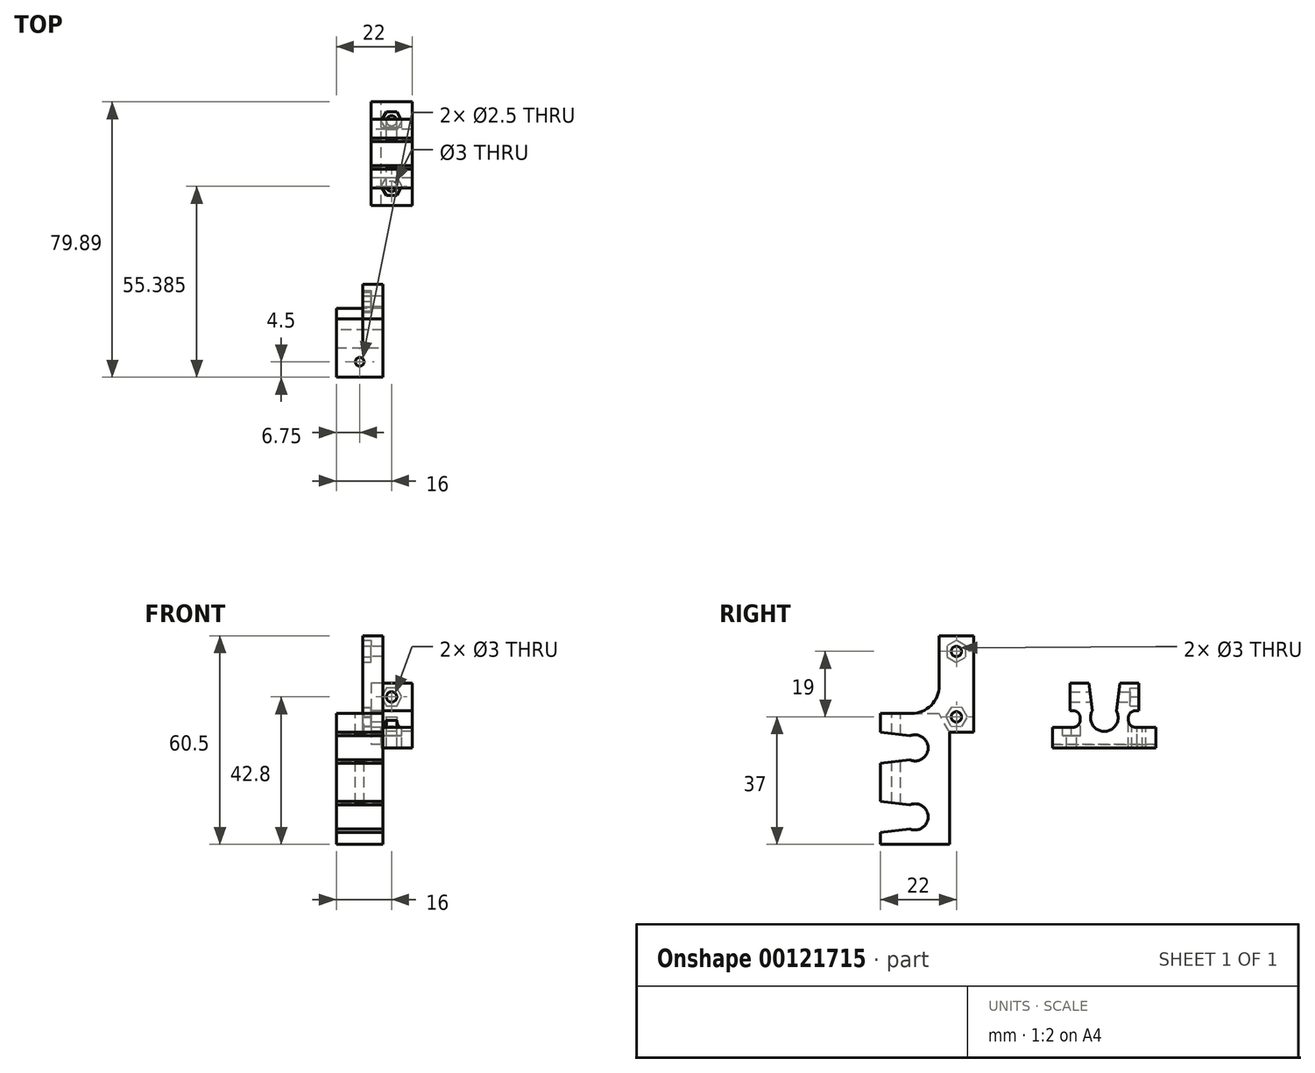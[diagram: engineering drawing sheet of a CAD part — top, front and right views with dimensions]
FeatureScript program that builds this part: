
annotation { "Feature Type Name" : "Feature", "Feature Type Description" : "" }
export const myFeature = defineFeature(function(context is Context, id is Id, definition is map)
    precondition{}
    {
        {
            var Q0;
            Q0=qCreatedBy(makeId("Right.planeOp"),FACE);
            var sketch = newSketch(context, id + "F0", { "sketchPlane" : qUnion([Q0])});
            skCircle(sketch, "E0", {"center": v(0, 0) * mm, "radius": 3.8 * mm});
            skCircle(sketch, "E1", {"center": v(0, -20) * mm, "radius": 3.8 * mm});
            skCircle(sketch, "E2", {"center": v(12, 9) * mm, "radius": 1.5 * mm});
            skCircle(sketch, "E3", {"center": v(12, 28) * mm, "radius": 1.5 * mm});
            skLineSegment(sketch, "E4", {"start": v(12, 28) * mm, "end": v(12, 9) * mm, "construction": true});
            skLineSegment(sketch, "E5.bottom", {"start": v(7, 32.5) * mm, "end": v(17, 32.5) * mm});
            skLineSegment(sketch, "E5.top", {"start": v(10, 4.5) * mm, "end": v(17, 4.5) * mm});
            skLineSegment(sketch, "E5.left", {"start": v(7, 32.5) * mm, "end": v(7, 18) * mm});
            skLineSegment(sketch, "E5.right", {"start": v(17, 32.5) * mm, "end": v(17, 4.5) * mm});
            skLineSegment(sketch, "E6.bottom", {"start": v(-10, 10) * mm, "end": v(-1, 10) * mm});
            skLineSegment(sketch, "E6.top", {"start": v(-10, -28) * mm, "end": v(10, -28) * mm});
            skLineSegment(sketch, "E6.left", {"start": v(-10, 10) * mm, "end": v(-10, -28) * mm});
            skLineSegment(sketch, "E6.right", {"start": v(10, 4.5) * mm, "end": v(10, -28) * mm});
            skPoint(sketch, "E7.visualSharp", {"position": v(7, 10) * mm});
            skArc(sketch, "E7.filletArc", {"start": v(-1, 10) * mm, "mid": v(4.66, 12.34) * mm, "end": v(7, 18) * mm});
            skLineSegment(sketch, "E8", {"start": v(0, 0) * mm, "end": v(0, -20) * mm, "construction": true});
            skSolve(sketch);
        }
        {
            var Q0;
            Q0 = qSketchRegion(id + "F0", true);
            extrude(context, id + "F1", {"entities" : qUnion([Q0]), "depth" : 3.5 * mm});
        }
        {
            var Q0;
            Q0=makeQuery(id+"F1.opExtrude","CAP_FACE",FACE,{"disambiguationData":[OSD([sQuery(id+"F0.wireOp",EDGE,"E0"),sQuery(id+"F0.wireOp",EDGE,"E1"),sQuery(id+"F0.wireOp",EDGE,"E2"),sQuery(id+"F0.wireOp",EDGE,"E3"),sQuery(id+"F0.wireOp",EDGE,"E5.bottom"),sQuery(id+"F0.wireOp",EDGE,"E5.top"),sQuery(id+"F0.wireOp",EDGE,"E5.left"),sQuery(id+"F0.wireOp",EDGE,"E5.right"),sQuery(id+"F0.wireOp",EDGE,"E6.bottom"),sQuery(id+"F0.wireOp",EDGE,"E6.top"),sQuery(id+"F0.wireOp",EDGE,"E6.left"),sQuery(id+"F0.wireOp",EDGE,"E6.right"),sQuery(id+"F0.wireOp",EDGE,"E7.filletArc")])],"isStart":true});
            var sketch = newSketch(context, id + "F2", { "sketchPlane" : qUnion([Q0])});
            skLineSegment(sketch, "E9.0", {"start": v(-10, 4.5) * mm, "end": v(-10, -28) * mm});
            skLineSegment(sketch, "E10.0", {"start": v(10, -28) * mm, "end": v(-10, -28) * mm});
            skLineSegment(sketch, "E11.0", {"start": v(10, 10) * mm, "end": v(10, -28) * mm});
            skLineSegment(sketch, "E12.0", {"start": v(10, 10) * mm, "end": v(1, 10) * mm});
            skCircle(sketch, "E13.0", {"center": v(0, -20) * mm, "radius": 3.8 * mm});
            skLineSegment(sketch, "E14", {"start": v(1, 10) * mm, "end": v(-7, 10) * mm});
            skLineSegment(sketch, "E15", {"start": v(-10, 4.5) * mm, "end": v(-7, 10) * mm});
            skLineSegment(sketch, "E16.0", {"start": v(-10, 4.5) * mm, "end": v(-17, 4.5) * mm});
            skLineSegment(sketch, "E17.0", {"start": v(-17, 32.5) * mm, "end": v(-17, 4.5) * mm});
            skLineSegment(sketch, "E18.0", {"start": v(-7, 32.5) * mm, "end": v(-17, 32.5) * mm});
            skLineSegment(sketch, "E19.0", {"start": v(-7, 32.5) * mm, "end": v(-7, 18) * mm});
            skArc(sketch, "E20.0", {"start": v(1, 10) * mm, "mid": v(-4.66, 12.34) * mm, "end": v(-7, 18) * mm});
            skCircle(sketch, "E21.0", {"center": v(-12, 9) * mm, "radius": 1.5 * mm});
            skCircle(sketch, "E22.0", {"center": v(-12, 28) * mm, "radius": 1.5 * mm});
            skCircle(sketch, "E23.cCircle", {"center": v(-12, 9) * mm, "radius": 2.75 * mm, "construction": true});
            skLineSegment(sketch, "E23.0", {"start": v(-8.83, 9.08) * mm, "end": v(-10.35, 6.29) * mm});
            skLineSegment(sketch, "E23.1", {"start": v(-10.35, 6.29) * mm, "end": v(-13.52, 6.21) * mm});
            skLineSegment(sketch, "E23.2", {"start": v(-13.52, 6.21) * mm, "end": v(-15.17, 8.92) * mm});
            skLineSegment(sketch, "E23.3", {"start": v(-15.17, 8.92) * mm, "end": v(-13.65, 11.71) * mm});
            skLineSegment(sketch, "E23.4", {"start": v(-13.65, 11.71) * mm, "end": v(-10.48, 11.79) * mm});
            skLineSegment(sketch, "E23.5", {"start": v(-10.48, 11.79) * mm, "end": v(-8.83, 9.08) * mm});
            skPoint(sketch, "E23.0.midPoint", {"position": v(-9.59, 7.68) * mm});
            skCircle(sketch, "E24.cCircle", {"center": v(-12, 28) * mm, "radius": 2.75 * mm, "construction": true});
            skLineSegment(sketch, "E24.0", {"start": v(-9.25, 29.59) * mm, "end": v(-9.25, 26.41) * mm});
            skLineSegment(sketch, "E24.1", {"start": v(-9.25, 26.41) * mm, "end": v(-12, 24.82) * mm});
            skLineSegment(sketch, "E24.2", {"start": v(-12, 24.82) * mm, "end": v(-14.75, 26.41) * mm});
            skLineSegment(sketch, "E24.3", {"start": v(-14.75, 26.41) * mm, "end": v(-14.75, 29.59) * mm});
            skLineSegment(sketch, "E24.4", {"start": v(-14.75, 29.59) * mm, "end": v(-12, 31.18) * mm});
            skLineSegment(sketch, "E24.5", {"start": v(-12, 31.18) * mm, "end": v(-9.25, 29.59) * mm});
            skPoint(sketch, "E24.0.midPoint", {"position": v(-9.25, 28) * mm});
            skSolve(sketch);
        }
        {
            var Q0;
            Q0=makeQuery(id+"F2.imprint","IMPRINT",FACE,{"disambiguationData":[TD([[makeQuery(id+"F2.imprint","IMPRINT",EDGE,{"derivedFrom":sQuery(id+"F2.wireOp",EDGE,"E14")}),-1.0]])]});
            extrude(context, id + "F3", {"entities" : qUnion([Q0]), "operationType" : NewBodyOperationType.ADD, "depth" : 2.3 * mm});
        }
        {
            var Q0;
            {var subQ0=sQuery(id+"F0.wireOp",EDGE,"E6.right");var subQ1=sQuery(id+"F0.wireOp",EDGE,"E0");var subQ2=sQuery(id+"F0.wireOp",EDGE,"E6.left");var subQ3=sQuery(id+"F0.wireOp",EDGE,"E6.top");var subQ4=sQuery(id+"F0.wireOp",EDGE,"E7.filletArc");var subQ5=sQuery(id+"F0.wireOp",EDGE,"E5.top");var subQ6=sQuery(id+"F0.wireOp",EDGE,"E1");var subQ7=sQuery(id+"F0.wireOp",EDGE,"E6.bottom");Q0=makeQuery(id+"F3.boolean.opBoolean","SPLIT",FACE,{"disambiguationData":[TD([makeQuery(id+"F1.opExtrude","SWEPT_FACE",FACE,{"disambiguationData":[OSD([subQ1])]})])],"derivedFrom":makeQuery(id+"F1.opExtrude","CAP_FACE",FACE,{"disambiguationData":[OSD([subQ1,subQ6,sQuery(id+"F0.wireOp",EDGE,"E2"),sQuery(id+"F0.wireOp",EDGE,"E3"),sQuery(id+"F0.wireOp",EDGE,"E5.bottom"),subQ5,sQuery(id+"F0.wireOp",EDGE,"E5.left"),sQuery(id+"F0.wireOp",EDGE,"E5.right"),subQ7,subQ3,subQ2,subQ0,subQ4])],"isStart":true})});}
            extrude(context, id + "F4", {"entities" : qUnion([Q0]), "operationType" : NewBodyOperationType.ADD, "depth" : 10 * mm});
        }
        {
            var Q0;
            Q0=makeQuery(id+"F1.opExtrude","CAP_FACE",FACE,{"disambiguationData":[OSD([sQuery(id+"F0.wireOp",EDGE,"E0"),sQuery(id+"F0.wireOp",EDGE,"E1"),sQuery(id+"F0.wireOp",EDGE,"E2"),sQuery(id+"F0.wireOp",EDGE,"E3"),sQuery(id+"F0.wireOp",EDGE,"E5.bottom"),sQuery(id+"F0.wireOp",EDGE,"E5.top"),sQuery(id+"F0.wireOp",EDGE,"E5.left"),sQuery(id+"F0.wireOp",EDGE,"E5.right"),sQuery(id+"F0.wireOp",EDGE,"E6.bottom"),sQuery(id+"F0.wireOp",EDGE,"E6.top"),sQuery(id+"F0.wireOp",EDGE,"E6.left"),sQuery(id+"F0.wireOp",EDGE,"E6.right"),sQuery(id+"F0.wireOp",EDGE,"E7.filletArc")])],"isStart":false});
            var sketch = newSketch(context, id + "F5", { "sketchPlane" : qUnion([Q0])});
            skLineSegment(sketch, "E25", {"start": v(0, 0) * mm, "end": v(-10, 0) * mm, "construction": true});
            skLineSegment(sketch, "E26", {"start": v(0, -20) * mm, "end": v(-10, -20) * mm, "construction": true});
            skCircle(sketch, "E27.0", {"center": v(0, 0) * mm, "radius": 3.8 * mm});
            skCircle(sketch, "E28.0", {"center": v(0, -20) * mm, "radius": 3.8 * mm});
            skLineSegment(sketch, "E29", {"start": v(-1.48, 3.5) * mm, "end": v(-10, 4.5) * mm});
            skLineSegment(sketch, "E30", {"start": v(-10, 4.5) * mm, "end": v(-10, -4.5) * mm});
            skLineSegment(sketch, "E31", {"start": v(-10, -4.5) * mm, "end": v(-1.48, -3.5) * mm});
            skLineSegment(sketch, "E32", {"start": v(-1.48, -16.5) * mm, "end": v(-10, -15.5) * mm});
            skLineSegment(sketch, "E33", {"start": v(-10, -15.5) * mm, "end": v(-10, -24.5) * mm});
            skLineSegment(sketch, "E34", {"start": v(-10, -24.5) * mm, "end": v(-1.48, -23.5) * mm});
            skLineSegment(sketch, "E35", {"start": v(-1.48, 3.5) * mm, "end": v(-1.48, -3.5) * mm});
            skLineSegment(sketch, "E36", {"start": v(-1.48, -16.5) * mm, "end": v(-1.48, -23.5) * mm});
            skSolve(sketch);
        }
        {
            var Q0;
            Q0 = qSketchRegion(id + "F5", true);
            extrude(context, id + "F6", {"entities" : qUnion([Q0]), "operationType" : NewBodyOperationType.REMOVE, "endBound" : BoundingType.THROUGH_ALL, "oppositeDirection" : true, "depth" : 25 * mm});
        }
        {
            var Q0;
            {var subQ0=sQuery(id+"F0.wireOp",EDGE,"E6.bottom");Q0=makeQuery(id+"F4.boolean.opBoolean","MERGE",FACE,{"derivedFrom":[makeQuery(id+"F1.opExtrude","SWEPT_FACE",FACE,{"disambiguationData":[OSD([subQ0])]}),makeQuery(id+"F4.opExtrude","SWEPT_FACE",FACE,{"disambiguationData":[OSD([subQ0,sQuery(id+"F2.wireOp",EDGE,"E14")])]})]});}
            var sketch = newSketch(context, id + "F7", { "sketchPlane" : qUnion([Q0])});
            skLineSegment(sketch, "E37", {"start": v(-3.25, -10) * mm, "end": v(-3.25, 7) * mm, "construction": true});
            skCircle(sketch, "E38", {"center": v(-3.25, -5.5) * mm, "radius": 3 * mm});
            skCircle(sketch, "E39", {"center": v(-3.25, -5.5) * mm, "radius": 1.25 * mm});
            skSolve(sketch);
        }
        {
            var Q0;
            Q0=makeQuery(id+"F7.imprint","IMPRINT",FACE,{"disambiguationData":[TD([[makeQuery(id+"F7.imprint","IMPRINT",EDGE,{"derivedFrom":sQuery(id+"F7.wireOp",EDGE,"E39")}),1.0]])]});
            extrude(context, id + "F8", {"entities" : qUnion([Q0]), "operationType" : NewBodyOperationType.REMOVE, "oppositeDirection" : true, "depth" : 30 * mm});
        }
        {
            var Q0;
            Q0=qCreatedBy(makeId("Right.planeOp"),FACE);
            var sketch = newSketch(context, id + "F9", { "sketchPlane" : qUnion([Q0])});
            skCircle(sketch, "E40", {"center": v(54.89, 8.8) * mm, "radius": 4 * mm});
            skLineSegment(sketch, "E41", {"start": v(54.89, 8.8) * mm, "end": v(54.89, 0) * mm, "construction": true});
            skLineSegment(sketch, "E42", {"start": v(69.89, 0) * mm, "end": v(39.89, 0) * mm});
            skLineSegment(sketch, "E43", {"start": v(39.89, 0) * mm, "end": v(39.89, 6) * mm});
            skLineSegment(sketch, "E44", {"start": v(39.89, 6) * mm, "end": v(47.89, 6) * mm});
            skLineSegment(sketch, "E45", {"start": v(61.89, 6) * mm, "end": v(69.89, 6) * mm});
            skLineSegment(sketch, "E46", {"start": v(69.89, 6) * mm, "end": v(69.89, 0) * mm});
            skLineSegment(sketch, "E47", {"start": v(47.89, 6) * mm, "end": v(47.89, 10.8) * mm});
            skLineSegment(sketch, "E48", {"start": v(47.89, 10.8) * mm, "end": v(44.89, 10.8) * mm});
            skLineSegment(sketch, "E49", {"start": v(44.89, 10.8) * mm, "end": v(44.89, 18.8) * mm});
            skLineSegment(sketch, "E50", {"start": v(44.89, 18.8) * mm, "end": v(64.89, 18.8) * mm});
            skLineSegment(sketch, "E51", {"start": v(64.89, 18.8) * mm, "end": v(64.89, 10.8) * mm});
            skLineSegment(sketch, "E52", {"start": v(64.89, 10.8) * mm, "end": v(61.89, 10.8) * mm});
            skLineSegment(sketch, "E53", {"start": v(61.89, 10.8) * mm, "end": v(61.89, 6) * mm});
            skSolve(sketch);
        }
        {
            var Q0;
            Q0 = qSketchRegion(id + "F9", true);
            extrude(context, id + "F10", {"entities" : qUnion([Q0]), "depth" : 12 * mm});
        }
        {
            var Q0;
            Q0=makeQuery(id+"F10.opExtrude","SWEPT_EDGE",EDGE,{"disambiguationData":[OSD([sQuery(id+"F9.wireOp",EDGE,"E44"),sQuery(id+"F9.wireOp",EDGE,"E47")])]});
            var Q1;
            Q1=makeQuery(id+"F10.opExtrude","SWEPT_EDGE",EDGE,{"disambiguationData":[OSD([sQuery(id+"F9.wireOp",EDGE,"E45"),sQuery(id+"F9.wireOp",EDGE,"E53")])]});
            fillet(context, id + "F11", {"entities" : qUnion([Q0, Q1]), "radius" : 2 * mm, "tangentPropagation" : true, "allowEdgeOverflow" : false});
        }
        {
            var Q0;
            Q0=makeQuery(id+"F10.opExtrude","SWEPT_FACE",FACE,{"disambiguationData":[OSD([sQuery(id+"F9.wireOp",EDGE,"E44")])]});
            var sketch = newSketch(context, id + "F12", { "sketchPlane" : qUnion([Q0])});
            skLineSegment(sketch, "E54", {"start": v(6, 39.89) * mm, "end": v(6, 69.89) * mm, "construction": true});
            skLineSegment(sketch, "E55", {"start": v(12.16, 54.89) * mm, "end": v(0, 54.89) * mm, "construction": true});
            skPoint(sketch, "E55.startSnap0", {"position": v(6, 54.89) * mm});
            skCircle(sketch, "E56", {"center": v(6, 45.39) * mm, "radius": 1.5 * mm});
            skCircle(sketch, "E57.cCircle", {"center": v(6, 45.39) * mm, "radius": 2.6 * mm, "construction": true});
            skLineSegment(sketch, "E57.0", {"start": v(9, 45.4) * mm, "end": v(7.5, 42.79) * mm});
            skLineSegment(sketch, "E57.1", {"start": v(7.5, 42.79) * mm, "end": v(4.5, 42.78) * mm});
            skLineSegment(sketch, "E57.2", {"start": v(4.5, 42.78) * mm, "end": v(3, 45.38) * mm});
            skLineSegment(sketch, "E57.3", {"start": v(3, 45.38) * mm, "end": v(4.5, 47.98) * mm});
            skLineSegment(sketch, "E57.4", {"start": v(4.5, 47.98) * mm, "end": v(7.5, 47.99) * mm});
            skLineSegment(sketch, "E57.5", {"start": v(7.5, 47.99) * mm, "end": v(9, 45.4) * mm});
            skPoint(sketch, "E57.0.midPoint", {"position": v(8.25, 44.1) * mm});
            skCircle(sketch, "E58.MirrorC", {"center": v(6, 64.39) * mm, "radius": 1.5 * mm});
            skCircle(sketch, "E59.MirrorC", {"center": v(6, 64.39) * mm, "radius": 2.6 * mm, "construction": true});
            skLineSegment(sketch, "E60.MirrorCS", {"start": v(3, 64.4) * mm, "end": v(4.5, 61.79) * mm});
            skLineSegment(sketch, "E61.MirrorCS", {"start": v(4.5, 61.79) * mm, "end": v(7.5, 61.78) * mm});
            skLineSegment(sketch, "E62.MirrorCS", {"start": v(7.5, 61.78) * mm, "end": v(9, 64.38) * mm});
            skLineSegment(sketch, "E63.MirrorCS", {"start": v(9, 64.38) * mm, "end": v(7.5, 66.98) * mm});
            skLineSegment(sketch, "E64.MirrorCS", {"start": v(7.5, 66.98) * mm, "end": v(4.5, 66.99) * mm});
            skLineSegment(sketch, "E65.MirrorCS", {"start": v(4.5, 66.99) * mm, "end": v(3, 64.4) * mm});
            skSolve(sketch);
        }
        {
            var Q0;
            Q0=makeQuery(id+"F12.imprint","IMPRINT",FACE,{"disambiguationData":[TD([[makeQuery(id+"F12.imprint","IMPRINT",EDGE,{"derivedFrom":sQuery(id+"F12.wireOp",EDGE,"E56")}),1.0]])]});
            var Q1;
            Q1=makeQuery(id+"F12.imprint","IMPRINT",FACE,{"disambiguationData":[TD([[makeQuery(id+"F12.imprint","IMPRINT",EDGE,{"derivedFrom":sQuery(id+"F12.wireOp",EDGE,"E58.MirrorC")}),-1.0]])]});
            var Q2;
            Q2=sQuery(id+"F12.wireOp",EDGE,"E56");
            var Q3;
            Q3=sQuery(id+"F12.wireOp",EDGE,"E58.MirrorC");
            extrude(context, id + "F13", {"entities" : qUnion([Q0, Q1]), "operationType" : NewBodyOperationType.REMOVE, "surfaceEntities" : qUnion([Q2, Q3]), "endBound" : BoundingType.THROUGH_ALL, "oppositeDirection" : true, "depth" : 25 * mm, "hasSecondDirection" : true, "secondDirectionOppositeDirection" : false, "secondDirectionDepth" : 3 * mm});
        }
        {
            var Q0;
            Q0 = qSketchRegion(id + "F12", true);
            extrude(context, id + "F14", {"entities" : qUnion([Q0]), "operationType" : NewBodyOperationType.REMOVE, "oppositeDirection" : true, "depth" : 2.5 * mm, "hasSecondDirection" : true, "secondDirectionOppositeDirection" : false, "secondDirectionDepth" : 2 * mm});
        }
        {
            var Q0;
            Q0=makeQuery(id+"F10.opExtrude","CAP_FACE",FACE,{"disambiguationData":[OSD([sQuery(id+"F9.wireOp",EDGE,"E40"),sQuery(id+"F9.wireOp",EDGE,"E42"),sQuery(id+"F9.wireOp",EDGE,"E43"),sQuery(id+"F9.wireOp",EDGE,"E44"),sQuery(id+"F9.wireOp",EDGE,"E45"),sQuery(id+"F9.wireOp",EDGE,"E46"),sQuery(id+"F9.wireOp",EDGE,"E47"),sQuery(id+"F9.wireOp",EDGE,"E48"),sQuery(id+"F9.wireOp",EDGE,"E49"),sQuery(id+"F9.wireOp",EDGE,"E50"),sQuery(id+"F9.wireOp",EDGE,"E51"),sQuery(id+"F9.wireOp",EDGE,"E52"),sQuery(id+"F9.wireOp",EDGE,"E53")])],"isStart":false});
            var sketch = newSketch(context, id + "F15", { "sketchPlane" : qUnion([Q0])});
            skCircle(sketch, "E66.0", {"center": v(54.89, 8.8) * mm, "radius": 4 * mm});
            skLineSegment(sketch, "E67.0", {"start": v(44.89, 18.8) * mm, "end": v(64.89, 18.8) * mm});
            skLineSegment(sketch, "E68", {"start": v(54.89, 8.8) * mm, "end": v(54.89, 18.8) * mm, "construction": true});
            skLineSegment(sketch, "E69", {"start": v(50.39, 18.8) * mm, "end": v(51.39, 10.74) * mm});
            skLineSegment(sketch, "E70.MirrorCS", {"start": v(59.39, 18.8) * mm, "end": v(58.39, 10.74) * mm});
            skSolve(sketch);
        }
        {
            var Q0;
            {var subQ0=sQuery(id+"F15.wireOp",EDGE,"E69");Q0=makeQuery(id+"F15.imprint","IMPRINT",FACE,{"disambiguationData":[TD([[makeQuery(id+"F15.imprint","IMPRINT",EDGE,{"derivedFrom":subQ0}),1.0]])]});}
            extrude(context, id + "F16", {"entities" : qUnion([Q0]), "operationType" : NewBodyOperationType.REMOVE, "endBound" : BoundingType.THROUGH_ALL, "oppositeDirection" : true, "depth" : 25 * mm});
        }
        {
            var Q0;
            Q0=makeQuery(id+"F10.opExtrude","SWEPT_FACE",FACE,{"disambiguationData":[OSD([sQuery(id+"F9.wireOp",EDGE,"E51")])]});
            var sketch = newSketch(context, id + "F17", { "sketchPlane" : qUnion([Q0])});
            skLineSegment(sketch, "E71", {"start": v(-6, 18.8) * mm, "end": v(-6, 10.8) * mm, "construction": true});
            skCircle(sketch, "E72", {"center": v(-6, 14.8) * mm, "radius": 1.5 * mm});
            skCircle(sketch, "E73.cCircle", {"center": v(-6, 14.8) * mm, "radius": 2.6 * mm, "construction": true});
            skLineSegment(sketch, "E73.0", {"start": v(-7.5, 17.4) * mm, "end": v(-4.5, 17.4) * mm});
            skLineSegment(sketch, "E73.1", {"start": v(-4.5, 17.4) * mm, "end": v(-3, 14.8) * mm});
            skLineSegment(sketch, "E73.2", {"start": v(-3, 14.8) * mm, "end": v(-4.5, 12.2) * mm});
            skLineSegment(sketch, "E73.3", {"start": v(-4.5, 12.2) * mm, "end": v(-7.5, 12.2) * mm});
            skLineSegment(sketch, "E73.4", {"start": v(-7.5, 12.2) * mm, "end": v(-9, 14.8) * mm});
            skLineSegment(sketch, "E73.5", {"start": v(-9, 14.8) * mm, "end": v(-7.5, 17.4) * mm});
            skPoint(sketch, "E73.0.midPoint", {"position": v(-6, 17.4) * mm});
            skSolve(sketch);
        }
        {
            var Q0;
            Q0=makeQuery(id+"F17.imprint","IMPRINT",FACE,{"disambiguationData":[TD([[makeQuery(id+"F17.imprint","IMPRINT",EDGE,{"derivedFrom":sQuery(id+"F17.wireOp",EDGE,"E72")}),1.0]])]});
            var Q1;
            Q1=sQuery(id+"F17.wireOp",EDGE,"E72");
            extrude(context, id + "F18", {"entities" : qUnion([Q0]), "operationType" : NewBodyOperationType.REMOVE, "surfaceEntities" : qUnion([Q1]), "endBound" : BoundingType.THROUGH_ALL, "oppositeDirection" : true, "depth" : 25 * mm});
        }
        {
            var Q0;
            Q0=makeQuery(id+"F17.imprint","IMPRINT",FACE,{"disambiguationData":[TD([[makeQuery(id+"F17.imprint","IMPRINT",EDGE,{"derivedFrom":sQuery(id+"F17.wireOp",EDGE,"E72")}),-1.0]])]});
            extrude(context, id + "F19", {"entities" : qUnion([Q0]), "operationType" : NewBodyOperationType.REMOVE, "oppositeDirection" : true, "depth" : 2.5 * mm});
        }
        {
            var Q0;
            Q0=makeQuery(id+"F10.opExtrude","SWEPT_EDGE",EDGE,{"disambiguationData":[OSD([sQuery(id+"F9.wireOp",EDGE,"E52"),sQuery(id+"F9.wireOp",EDGE,"E53")])]});
            var Q1;
            Q1=makeQuery(id+"F10.opExtrude","SWEPT_EDGE",EDGE,{"disambiguationData":[OSD([sQuery(id+"F9.wireOp",EDGE,"E47"),sQuery(id+"F9.wireOp",EDGE,"E48")])]});
            fillet(context, id + "F20", {"entities" : qUnion([Q0, Q1]), "radius" : 2 * mm, "tangentPropagation" : true, "allowEdgeOverflow" : false});
        }
        {
            var Q0;
            Q0=makeQuery(id+"F10.opExtrude","SWEPT_FACE",FACE,{"disambiguationData":[OSD([sQuery(id+"F9.wireOp",EDGE,"E42")])]});
            var sketch = newSketch(context, id + "F21", { "sketchPlane" : qUnion([Q0])});
            skLineSegment(sketch, "E74.0", {"start": v(0, -69.89) * mm, "end": v(0, -39.89) * mm});
            skLineSegment(sketch, "E75.0", {"start": v(3, -69.89) * mm, "end": v(0, -69.89) * mm});
            skLineSegment(sketch, "E76.0", {"start": v(3, -39.89) * mm, "end": v(0, -39.89) * mm});
            skLineSegment(sketch, "E77", {"start": v(3, -39.89) * mm, "end": v(3, -69.89) * mm});
            skPoint(sketch, "E78.orphan", {"position": v(12, -39.89) * mm});
            skPoint(sketch, "E79.orphan", {"position": v(12, -69.89) * mm});
            skSolve(sketch);
        }
        {
            var Q0;
            Q0=makeQuery(id+"F21.imprint","IMPRINT",FACE,{"disambiguationData":[TD([[makeQuery(id+"F21.imprint","IMPRINT",EDGE,{"derivedFrom":sQuery(id+"F21.wireOp",EDGE,"E74.0")}),-1.0]])]});
            extrude(context, id + "F22", {"entities" : qUnion([Q0]), "operationType" : NewBodyOperationType.REMOVE, "oppositeDirection" : true, "depth" : 1 * mm});
        }
    });
